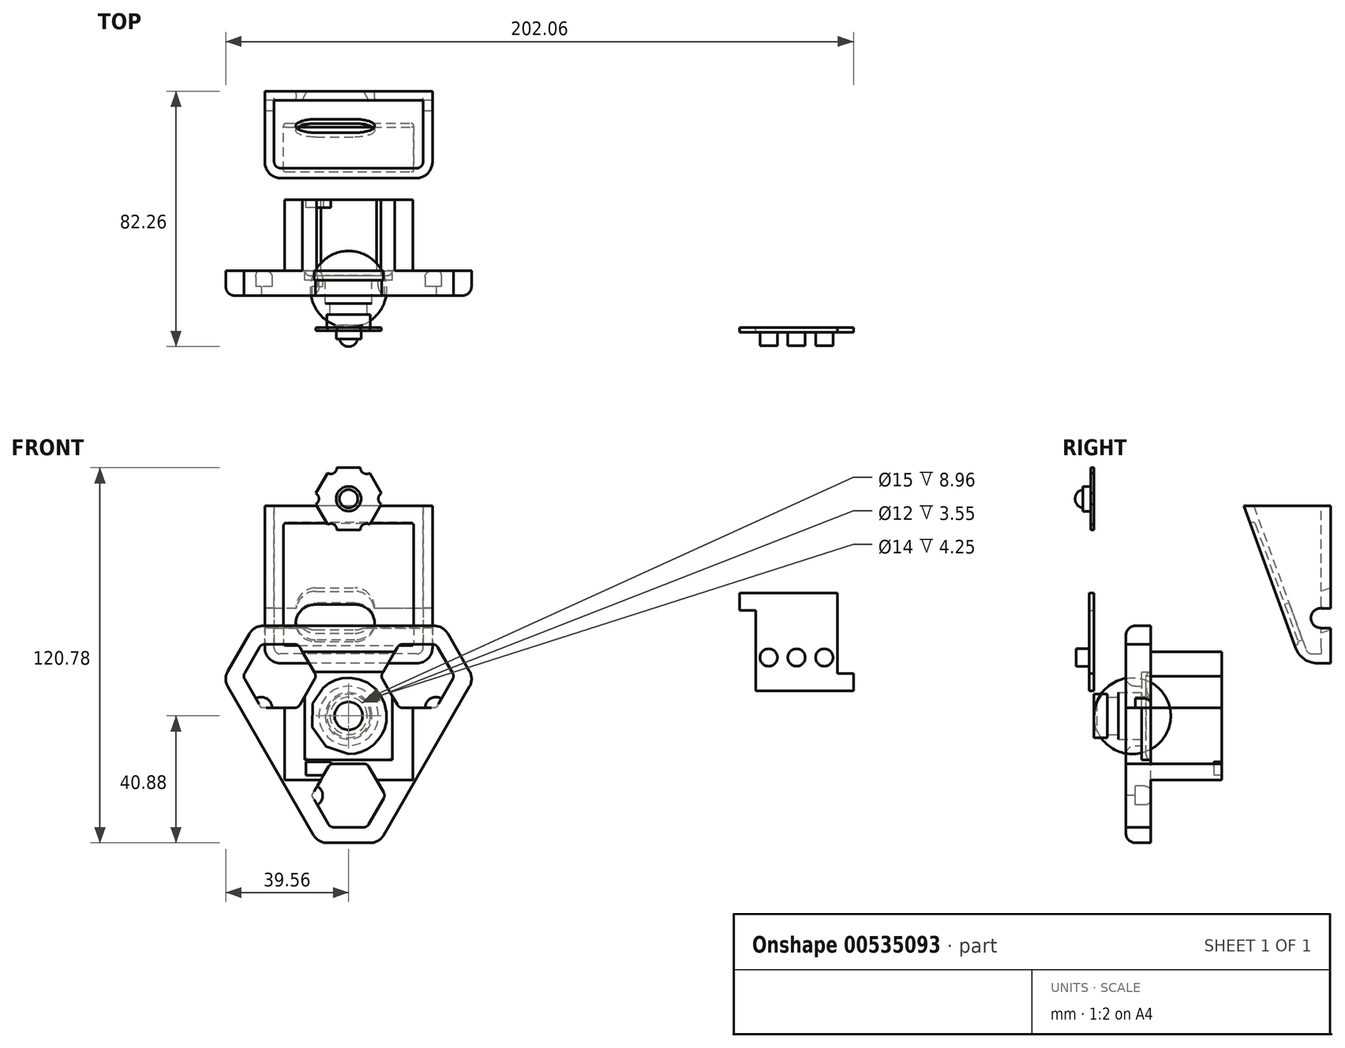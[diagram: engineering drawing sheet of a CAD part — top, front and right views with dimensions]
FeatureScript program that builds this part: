
annotation { "Feature Type Name" : "Feature", "Feature Type Description" : "" }
export const myFeature = defineFeature(function(context is Context, id is Id, definition is map)
    precondition{}
    {
        {
            var Q0;
            Q0=qCreatedBy(makeId("Right.planeOp"),FACE);
            var sketch = newSketch(context, id + "F0", { "sketchPlane" : qUnion([Q0])});
            skLineSegment(sketch, "E0", {"start": v(0, 4.5) * mm, "end": v(0, 7) * mm});
            skLineSegment(sketch, "E1", {"start": v(0, 7) * mm, "end": v(4.25, 7) * mm});
            skLineSegment(sketch, "E2", {"start": v(4.25, 7) * mm, "end": v(4.25, 6) * mm});
            skLineSegment(sketch, "E3", {"start": v(4.25, 6) * mm, "end": v(7.8, 6) * mm});
            skLineSegment(sketch, "E4", {"start": v(7.8, 6) * mm, "end": v(7.8, 7.5) * mm});
            skLineSegment(sketch, "E5", {"start": v(7.8, 7.5) * mm, "end": v(16.76, 7.5) * mm});
            skLineSegment(sketch, "E6", {"start": v(16.76, 7.5) * mm, "end": v(16.76, 0) * mm});
            skLineSegment(sketch, "E7", {"start": v(16.76, 0) * mm, "end": v(0, 0) * mm});
            skArc(sketch, "E8", {"start": v(0, 0) * mm, "mid": v(0.2, 2.29) * mm, "end": v(0.82, 4.5) * mm});
            skLineSegment(sketch, "E9", {"start": v(0.82, 4.5) * mm, "end": v(0, 4.5) * mm});
            skSolve(sketch);
        }
        {
            var Q0;
            Q0=qSketchRegion(id+"F0",true);
            var Q1;
            Q1=sQuery(id+"F0.wireOp",EDGE,"E7");
            revolve(context, id + "F1", {"entities" : qUnion([Q0]), "axis" : qUnion([Q1]), "revolveType" : RevolveType.FULL});
        }
        {
            var Q0;
            Q0=makeQuery(id+"F1.opRevolve","SWEPT_FACE",FACE,{"disambiguationData":[OSD([sQuery(id+"F0.wireOp",EDGE,"E6")])]});
            var sketch = newSketch(context, id + "F2", { "sketchPlane" : qUnion([Q0])});
            skLineSegment(sketch, "E10.bottom", {"start": v(14.1, -14.1) * mm, "end": v(-14.1, -14.1) * mm});
            skLineSegment(sketch, "E10.top", {"start": v(14.1, 14.1) * mm, "end": v(-14.1, 14.1) * mm});
            skLineSegment(sketch, "E10.left", {"start": v(14.1, -14.1) * mm, "end": v(14.1, 14.1) * mm});
            skLineSegment(sketch, "E10.right", {"start": v(-14.1, -14.1) * mm, "end": v(-14.1, 14.1) * mm});
            skPoint(sketch, "E10.middle", {"position": v(0, 0) * mm});
            skSolve(sketch);
        }
        {
            var Q0;
            Q0=qSketchRegion(id+"F2",true);
            extrude(context, id + "F3", {"entities" : qUnion([Q0]), "operationType" : NewBodyOperationType.ADD, "depth" : 1.5 * mm});
        }
        {
            var Q0;
            Q0=qCreatedBy(makeId("Front.planeOp"),FACE);
            var sketch = newSketch(context, id + "F4", { "sketchPlane" : qUnion([Q0])});
            skCircle(sketch, "E11.cCircle", {"center": v(0, 69.9) * mm, "radius": 11.55 * mm, "construction": true});
            skLineSegment(sketch, "E11.0", {"start": v(5.77, 59.9) * mm, "end": v(-5.77, 59.9) * mm});
            skLineSegment(sketch, "E11.1", {"start": v(-5.77, 59.9) * mm, "end": v(-11.55, 69.9) * mm});
            skLineSegment(sketch, "E11.2", {"start": v(-11.55, 69.9) * mm, "end": v(-5.77, 79.9) * mm});
            skLineSegment(sketch, "E11.3", {"start": v(-5.77, 79.9) * mm, "end": v(5.77, 79.9) * mm});
            skLineSegment(sketch, "E11.4", {"start": v(5.77, 79.9) * mm, "end": v(11.55, 69.9) * mm});
            skLineSegment(sketch, "E11.5", {"start": v(11.55, 69.9) * mm, "end": v(5.77, 59.9) * mm});
            skCircle(sketch, "E12", {"center": v(-5.77, 79.9) * mm, "radius": 2 * mm});
            skCircle(sketch, "E13", {"center": v(5.77, 79.9) * mm, "radius": 2 * mm});
            skCircle(sketch, "E14", {"center": v(11.55, 69.9) * mm, "radius": 2 * mm});
            skCircle(sketch, "E15", {"center": v(5.77, 59.9) * mm, "radius": 2 * mm});
            skCircle(sketch, "E16", {"center": v(-5.77, 59.9) * mm, "radius": 2 * mm});
            skCircle(sketch, "E17", {"center": v(-11.55, 69.9) * mm, "radius": 2 * mm});
            skSolve(sketch);
        }
        {
            var Q0;
            {var subQ13=sQuery(id+"F4.wireOp",EDGE,"E15");var subQ15=sQuery(id+"F4.wireOp",EDGE,"E11.0");var subQ16=makeQuery(id+"F4.imprint","INTERSECT",VERTEX,{"derivedFrom":[subQ15,subQ13]});Q0=makeQuery(id+"F4.imprint","IMPRINT",FACE,{"disambiguationData":[TD([[makeQuery(id+"F4.imprint","IMPRINT",EDGE,{"disambiguationData":[TD([[subQ16,-1.0]])],"derivedFrom":subQ15}),-1.0]])]});}
            extrude(context, id + "F5", {"entities" : qUnion([Q0]), "depth" : 1.02 * mm});
        }
        {
            var Q0;
            Q0=makeQuery(id+"F3.opExtrude","CAP_FACE",FACE,{"disambiguationData":[OSD([sQuery(id+"F2.wireOp",EDGE,"E10.bottom"),sQuery(id+"F2.wireOp",EDGE,"E10.top"),sQuery(id+"F2.wireOp",EDGE,"E10.left"),sQuery(id+"F2.wireOp",EDGE,"E10.right")])],"isStart":false});
            var sketch = newSketch(context, id + "F6", { "sketchPlane" : qUnion([Q0])});
            skLineSegment(sketch, "E18.bottom", {"start": v(-20.64, -20.64) * mm, "end": v(20.64, -20.64) * mm});
            skLineSegment(sketch, "E18.top", {"start": v(-20.64, 20.64) * mm, "end": v(20.64, 20.64) * mm});
            skLineSegment(sketch, "E18.left", {"start": v(-20.64, -20.64) * mm, "end": v(-20.64, 20.64) * mm});
            skLineSegment(sketch, "E18.right", {"start": v(20.64, -20.64) * mm, "end": v(20.64, 20.64) * mm});
            skPoint(sketch, "E18.middle", {"position": v(0, 0) * mm});
            skSolve(sketch);
        }
        {
            var Q0;
            Q0=qSketchRegion(id+"F6",true);
            extrude(context, id + "F7", {"entities" : qUnion([Q0]), "operationType" : NewBodyOperationType.ADD, "depth" : 22.86 * mm});
        }
        {
            var Q0;
            Q0=makeQuery(id+"F3.opExtrude","SWEPT_EDGE",EDGE,{"disambiguationData":[OSD([sQuery(id+"F2.wireOp",EDGE,"E10.top"),sQuery(id+"F2.wireOp",EDGE,"E10.right")])]});
            var Q1;
            Q1=makeQuery(id+"F3.opExtrude","SWEPT_EDGE",EDGE,{"disambiguationData":[OSD([sQuery(id+"F2.wireOp",EDGE,"E10.top"),sQuery(id+"F2.wireOp",EDGE,"E10.left")])]});
            var Q2;
            Q2=makeQuery(id+"F3.opExtrude","SWEPT_EDGE",EDGE,{"disambiguationData":[OSD([sQuery(id+"F2.wireOp",EDGE,"E10.bottom"),sQuery(id+"F2.wireOp",EDGE,"E10.right")])]});
            var Q3;
            Q3=makeQuery(id+"F3.opExtrude","SWEPT_EDGE",EDGE,{"disambiguationData":[OSD([sQuery(id+"F2.wireOp",EDGE,"E10.bottom"),sQuery(id+"F2.wireOp",EDGE,"E10.left")])]});
            fillet(context, id + "F8", {"entities" : qUnion([Q0, Q1, Q2, Q3]), "radius" : 1.59 * mm, "tangentPropagation" : true, "allowEdgeOverflow" : false});
        }
        {
            var Q0;
            Q0=makeQuery(id+"F3.opExtrude","CAP_EDGE",EDGE,{"disambiguationData":[OSD([sQuery(id+"F2.wireOp",EDGE,"E10.bottom")])],"isStart":true});
            fillet(context, id + "F9", {"entities" : qUnion([Q0]), "radius" : 1.59 * mm, "tangentPropagation" : true, "allowEdgeOverflow" : false});
        }
        {
            var Q0;
            Q0=makeQuery(id+"F7.opExtrude","CAP_FACE",FACE,{"disambiguationData":[OSD([sQuery(id+"F6.wireOp",EDGE,"E18.bottom"),sQuery(id+"F6.wireOp",EDGE,"E18.top"),sQuery(id+"F6.wireOp",EDGE,"E18.left"),sQuery(id+"F6.wireOp",EDGE,"E18.right")])],"isStart":false});
            var sketch = newSketch(context, id + "F10", { "sketchPlane" : qUnion([Q0])});
            skLineSegment(sketch, "E19.bottom", {"start": v(5.69, -14.77) * mm, "end": v(13.73, -14.77) * mm});
            skLineSegment(sketch, "E19.top", {"start": v(5.69, -19.15) * mm, "end": v(13.73, -19.15) * mm});
            skLineSegment(sketch, "E19.left", {"start": v(5.69, -14.77) * mm, "end": v(5.69, -19.15) * mm});
            skLineSegment(sketch, "E19.right", {"start": v(13.73, -14.77) * mm, "end": v(13.73, -19.15) * mm});
            skSolve(sketch);
        }
        {
            var Q0;
            Q0=qSketchRegion(id+"F10",true);
            extrude(context, id + "F11", {"entities" : qUnion([Q0]), "operationType" : NewBodyOperationType.REMOVE, "oppositeDirection" : true, "depth" : 2.54 * mm});
        }
        {
            var Q0;
            Q0=qCreatedBy(makeId("Right.planeOp"),FACE);
            var sketch = newSketch(context, id + "F12", { "sketchPlane" : qUnion([Q0])});
            skLineSegment(sketch, "E20", {"start": v(-6.12, 69.9) * mm, "end": v(-1.02, 69.9) * mm});
            skLineSegment(sketch, "E21", {"start": v(-1.02, 69.9) * mm, "end": v(-1.02, 73.9) * mm});
            skLineSegment(sketch, "E22", {"start": v(-1.02, 73.9) * mm, "end": v(-3.62, 73.9) * mm});
            skLineSegment(sketch, "E23", {"start": v(-3.62, 73.9) * mm, "end": v(-3.62, 72.85) * mm});
            skArc(sketch, "E24", {"start": v(-6.12, 69.9) * mm, "mid": v(-5.4, 71.83) * mm, "end": v(-3.62, 72.85) * mm});
            skSolve(sketch);
        }
        {
            var Q0;
            Q0=makeQuery(id+"F12.imprint","IMPRINT",FACE,{"disambiguationData":[TD([[makeQuery(id+"F12.imprint","IMPRINT",EDGE,{"derivedFrom":sQuery(id+"F12.wireOp",EDGE,"E20")}),1.0]])]});
            var Q1;
            Q1=sQuery(id+"F12.wireOp",EDGE,"E20");
            revolve(context, id + "F13", {"operationType" : NewBodyOperationType.ADD, "entities" : qUnion([Q0]), "axis" : qUnion([Q1]), "revolveType" : RevolveType.FULL});
        }
        {
            var Q0;
            Q0=makeQuery(id+"F7.opExtrude","CAP_FACE",FACE,{"disambiguationData":[OSD([sQuery(id+"F6.wireOp",EDGE,"E18.bottom"),sQuery(id+"F6.wireOp",EDGE,"E18.top"),sQuery(id+"F6.wireOp",EDGE,"E18.left"),sQuery(id+"F6.wireOp",EDGE,"E18.right")])],"isStart":true});
            var sketch = newSketch(context, id + "F14", { "sketchPlane" : qUnion([Q0])});
            skLineSegment(sketch, "E25.bottom", {"start": v(14.1, -14.1) * mm, "end": v(-14.1, -14.1) * mm});
            skLineSegment(sketch, "E25.top", {"start": v(14.1, 14.1) * mm, "end": v(-14.1, 14.1) * mm});
            skLineSegment(sketch, "E25.left", {"start": v(14.1, -14.1) * mm, "end": v(14.1, 14.1) * mm});
            skLineSegment(sketch, "E25.right", {"start": v(-14.1, -14.1) * mm, "end": v(-14.1, 14.1) * mm});
            skPoint(sketch, "E25.middle", {"position": v(0, 0) * mm});
            skLineSegment(sketch, "E26", {"start": v(-30.48, 28.97) * mm, "end": v(-40.33, 11.92) * mm});
            skLineSegment(sketch, "E27", {"start": v(-40.33, 11.92) * mm, "end": v(-9.84, -40.88) * mm});
            skLineSegment(sketch, "E28", {"start": v(-9.84, -40.88) * mm, "end": v(9.84, -40.88) * mm});
            skLineSegment(sketch, "E29", {"start": v(9.84, -40.88) * mm, "end": v(40.33, 11.92) * mm});
            skLineSegment(sketch, "E30", {"start": v(40.33, 11.92) * mm, "end": v(30.48, 28.97) * mm});
            skLineSegment(sketch, "E31", {"start": v(30.48, 28.97) * mm, "end": v(-30.48, 28.97) * mm});
            skLineSegment(sketch, "E32", {"start": v(-35.4, 20.44) * mm, "end": v(25.09, -14.48) * mm, "construction": true});
            skCircle(sketch, "E33.cCircle", {"center": v(-20.64, 11.92) * mm, "radius": 12.28 * mm, "construction": true});
            skLineSegment(sketch, "E33.0", {"start": v(-32.92, 11.92) * mm, "end": v(-26.78, 22.55) * mm, "construction": true});
            skLineSegment(sketch, "E33.1", {"start": v(-26.78, 22.55) * mm, "end": v(-14.5, 22.55) * mm, "construction": true});
            skLineSegment(sketch, "E33.2", {"start": v(-14.5, 22.55) * mm, "end": v(-8.36, 11.92) * mm, "construction": true});
            skLineSegment(sketch, "E33.3", {"start": v(-8.36, 11.92) * mm, "end": v(-14.5, 1.28) * mm, "construction": true});
            skLineSegment(sketch, "E33.4", {"start": v(-14.5, 1.28) * mm, "end": v(-26.78, 1.28) * mm, "construction": true});
            skLineSegment(sketch, "E33.5", {"start": v(-26.78, 1.28) * mm, "end": v(-32.92, 11.92) * mm, "construction": true});
            skLineSegment(sketch, "E34", {"start": v(-40.33, 11.92) * mm, "end": v(-20.64, 11.92) * mm, "construction": true});
            skSolve(sketch);
        }
        {
            var Q0;
            Q0=makeQuery(id+"F14.imprint","IMPRINT",FACE,{"disambiguationData":[TD([[makeQuery(id+"F14.imprint","IMPRINT",EDGE,{"derivedFrom":sQuery(id+"F14.wireOp",EDGE,"E26")}),1.0]])]});
            extrude(context, id + "F15", {"entities" : qUnion([Q0]), "depth" : 3 * mm});
        }
        {
            var Q0;
            Q0=makeQuery(id+"F15.opExtrude","CAP_FACE",FACE,{"disambiguationData":[OSD([sQuery(id+"F6.wireOp",EDGE,"E18.bottom"),sQuery(id+"F6.wireOp",EDGE,"E18.top"),sQuery(id+"F6.wireOp",EDGE,"E18.left"),sQuery(id+"F6.wireOp",EDGE,"E18.right"),sQuery(id+"F14.wireOp",EDGE,"E26"),sQuery(id+"F14.wireOp",EDGE,"E27"),sQuery(id+"F14.wireOp",EDGE,"E28"),sQuery(id+"F14.wireOp",EDGE,"E29"),sQuery(id+"F14.wireOp",EDGE,"E30"),sQuery(id+"F14.wireOp",EDGE,"E31")])],"isStart":false});
            var sketch = newSketch(context, id + "F16", { "sketchPlane" : qUnion([Q0])});
            skLineSegment(sketch, "E35.0", {"start": v(-30.48, 28.97) * mm, "end": v(-40.33, 11.92) * mm});
            skLineSegment(sketch, "E36.0", {"start": v(30.48, 28.97) * mm, "end": v(-30.48, 28.97) * mm});
            skLineSegment(sketch, "E37.0", {"start": v(-40.33, 11.92) * mm, "end": v(-9.84, -40.88) * mm});
            skLineSegment(sketch, "E38.0", {"start": v(40.33, 11.92) * mm, "end": v(30.48, 28.97) * mm});
            skLineSegment(sketch, "E39.0", {"start": v(9.84, -40.88) * mm, "end": v(40.33, 11.92) * mm});
            skLineSegment(sketch, "E40.0", {"start": v(-9.84, -40.88) * mm, "end": v(9.84, -40.88) * mm});
            skCircle(sketch, "E41", {"center": v(0, 0) * mm, "radius": 9.53 * mm});
            skSolve(sketch);
        }
        {
            var Q0;
            Q0=qSketchRegion(id+"F16",true);
            var Q1;
            {var subQ4=sQuery(id+"F6.wireOp",EDGE,"E18.bottom");Q1=makeQuery(id+"F14.imprint","IMPRINT",FACE,{"disambiguationData":[TD([[makeQuery(id+"F14.imprint","IMPRINT",EDGE,{"derivedFrom":makeQuery(id+"F7.opExtrude","CAP_EDGE",EDGE,{"disambiguationData":[OSD([subQ4])],"isStart":true})}),-1.0]])]});}
            extrude(context, id + "F17", {"entities" : qUnion([Q0, Q1]), "operationType" : NewBodyOperationType.ADD, "depth" : 5 * mm, "offsetDistance" : 25.4 * mm});
        }
        {
            var Q0;
            Q0=makeQuery(id+"F17.opExtrude","CAP_FACE",FACE,{"disambiguationData":[OSD([sQuery(id+"F16.wireOp",EDGE,"E35.0"),sQuery(id+"F16.wireOp",EDGE,"E36.0"),sQuery(id+"F16.wireOp",EDGE,"E37.0"),sQuery(id+"F16.wireOp",EDGE,"E38.0"),sQuery(id+"F16.wireOp",EDGE,"E39.0"),sQuery(id+"F16.wireOp",EDGE,"E40.0"),sQuery(id+"F16.wireOp",EDGE,"E41")])],"isStart":false});
            var sketch = newSketch(context, id + "F18", { "sketchPlane" : qUnion([Q0])});
            skCircle(sketch, "E42.cCircle", {"center": v(-22.2, 12.82) * mm, "radius": 11.84 * mm, "construction": true});
            skLineSegment(sketch, "E42.0", {"start": v(-34.04, 12.82) * mm, "end": v(-28.12, 23.07) * mm});
            skLineSegment(sketch, "E42.1", {"start": v(-28.12, 23.07) * mm, "end": v(-16.28, 23.07) * mm});
            skLineSegment(sketch, "E42.2", {"start": v(-16.28, 23.07) * mm, "end": v(-10.36, 12.82) * mm});
            skLineSegment(sketch, "E42.3", {"start": v(-10.36, 12.82) * mm, "end": v(-16.28, 2.57) * mm});
            skLineSegment(sketch, "E42.4", {"start": v(-16.28, 2.57) * mm, "end": v(-28.12, 2.57) * mm});
            skLineSegment(sketch, "E42.5", {"start": v(-28.12, 2.57) * mm, "end": v(-34.04, 12.82) * mm});
            skLineSegment(sketch, "E43", {"start": v(-35.4, 20.44) * mm, "end": v(25.09, -14.48) * mm, "construction": true});
            skCircle(sketch, "E44.cCircle", {"center": v(22.2, 12.82) * mm, "radius": 11.84 * mm, "construction": true});
            skLineSegment(sketch, "E44.0", {"start": v(16.28, 23.07) * mm, "end": v(28.12, 23.07) * mm});
            skLineSegment(sketch, "E44.1", {"start": v(28.12, 23.07) * mm, "end": v(34.04, 12.82) * mm});
            skLineSegment(sketch, "E44.2", {"start": v(34.04, 12.82) * mm, "end": v(28.12, 2.57) * mm});
            skLineSegment(sketch, "E44.3", {"start": v(28.12, 2.57) * mm, "end": v(16.28, 2.57) * mm});
            skLineSegment(sketch, "E44.4", {"start": v(16.28, 2.57) * mm, "end": v(10.36, 12.82) * mm});
            skLineSegment(sketch, "E44.5", {"start": v(10.36, 12.82) * mm, "end": v(16.28, 23.07) * mm});
            skCircle(sketch, "E45.cCircle", {"center": v(0, -25.63) * mm, "radius": 11.84 * mm, "construction": true});
            skLineSegment(sketch, "E45.0", {"start": v(11.84, -25.63) * mm, "end": v(5.92, -35.88) * mm});
            skLineSegment(sketch, "E45.1", {"start": v(5.92, -35.88) * mm, "end": v(-5.92, -35.88) * mm});
            skLineSegment(sketch, "E45.2", {"start": v(-5.92, -35.88) * mm, "end": v(-11.84, -25.63) * mm});
            skLineSegment(sketch, "E45.3", {"start": v(-11.84, -25.63) * mm, "end": v(-5.92, -15.38) * mm});
            skLineSegment(sketch, "E45.4", {"start": v(-5.92, -15.38) * mm, "end": v(5.92, -15.38) * mm});
            skLineSegment(sketch, "E45.5", {"start": v(5.92, -15.38) * mm, "end": v(11.84, -25.63) * mm});
            skArc(sketch, "E46", {"start": v(-19.78, 23.07) * mm, "mid": v(-18.03, 20.04) * mm, "end": v(-14.53, 20.04) * mm});
            skArc(sketch, "E47", {"start": v(-29.87, 5.6) * mm, "mid": v(-26.37, 5.6) * mm, "end": v(-24.62, 2.57) * mm});
            skArc(sketch, "E48", {"start": v(14.53, 20.04) * mm, "mid": v(18.03, 20.04) * mm, "end": v(19.78, 23.07) * mm});
            skArc(sketch, "E49", {"start": v(24.62, 2.57) * mm, "mid": v(26.37, 5.6) * mm, "end": v(29.87, 5.6) * mm});
            skArc(sketch, "E50", {"start": v(10.09, -22.6) * mm, "mid": v(8.34, -25.63) * mm, "end": v(10.09, -28.66) * mm});
            skArc(sketch, "E51", {"start": v(-10.09, -22.6) * mm, "mid": v(-8.34, -25.63) * mm, "end": v(-10.09, -28.66) * mm});
            skSolve(sketch);
        }
        {
            var Q0;
            Q0=qSketchRegion(id+"F18",true);
            extrude(context, id + "F19", {"entities" : qUnion([Q0]), "operationType" : NewBodyOperationType.REMOVE, "oppositeDirection" : true, "depth" : 3 * mm});
        }
        {
            var Q0;
            {var subQ3=sQuery(id+"F18.wireOp",EDGE,"E46");Q0=makeQuery(id+"F18.imprint","IMPRINT",FACE,{"disambiguationData":[TD([[makeQuery(id+"F18.imprint","IMPRINT",EDGE,{"derivedFrom":subQ3}),1.0]])]});}
            var Q1;
            {var subQ3=sQuery(id+"F18.wireOp",EDGE,"E47");Q1=makeQuery(id+"F18.imprint","IMPRINT",FACE,{"disambiguationData":[TD([[makeQuery(id+"F18.imprint","IMPRINT",EDGE,{"derivedFrom":subQ3}),-1.0]])]});}
            var Q2;
            {var subQ3=sQuery(id+"F18.wireOp",EDGE,"E48");Q2=makeQuery(id+"F18.imprint","IMPRINT",FACE,{"disambiguationData":[TD([[makeQuery(id+"F18.imprint","IMPRINT",EDGE,{"derivedFrom":subQ3}),1.0]])]});}
            var Q3;
            {var subQ3=sQuery(id+"F18.wireOp",EDGE,"E49");Q3=makeQuery(id+"F18.imprint","IMPRINT",FACE,{"disambiguationData":[TD([[makeQuery(id+"F18.imprint","IMPRINT",EDGE,{"derivedFrom":subQ3}),-1.0]])]});}
            var Q4;
            {var subQ3=sQuery(id+"F18.wireOp",EDGE,"E50");Q4=makeQuery(id+"F18.imprint","IMPRINT",FACE,{"disambiguationData":[TD([[makeQuery(id+"F18.imprint","IMPRINT",EDGE,{"derivedFrom":subQ3}),1.0]])]});}
            var Q5;
            {var subQ3=sQuery(id+"F18.wireOp",EDGE,"E51");Q5=makeQuery(id+"F18.imprint","IMPRINT",FACE,{"disambiguationData":[TD([[makeQuery(id+"F18.imprint","IMPRINT",EDGE,{"derivedFrom":subQ3}),-1.0]])]});}
            extrude(context, id + "F20", {"entities" : qUnion([Q0, Q1, Q2, Q3, Q4, Q5]), "operationType" : NewBodyOperationType.REMOVE, "endBound" : BoundingType.THROUGH_ALL, "oppositeDirection" : true, "depth" : 25.4 * mm});
        }
        {
            var Q0;
            Q0=makeQuery(id+"F17.boolean.opBoolean","MERGE",EDGE,{"derivedFrom":[makeQuery(id+"F15.opExtrude","SWEPT_EDGE",EDGE,{"disambiguationData":[OSD([sQuery(id+"F14.wireOp",EDGE,"E26"),sQuery(id+"F14.wireOp",EDGE,"E31")])]}),makeQuery(id+"F17.opExtrude","SWEPT_EDGE",EDGE,{"disambiguationData":[OSD([sQuery(id+"F16.wireOp",EDGE,"E35.0"),sQuery(id+"F16.wireOp",EDGE,"E36.0")])]})]});
            var Q1;
            Q1=makeQuery(id+"F17.boolean.opBoolean","MERGE",EDGE,{"derivedFrom":[makeQuery(id+"F15.opExtrude","SWEPT_EDGE",EDGE,{"disambiguationData":[OSD([sQuery(id+"F14.wireOp",EDGE,"E26"),sQuery(id+"F14.wireOp",EDGE,"E27")])]}),makeQuery(id+"F17.opExtrude","SWEPT_EDGE",EDGE,{"disambiguationData":[OSD([sQuery(id+"F16.wireOp",EDGE,"E35.0"),sQuery(id+"F16.wireOp",EDGE,"E37.0")])]})]});
            var Q2;
            Q2=makeQuery(id+"F17.boolean.opBoolean","MERGE",EDGE,{"derivedFrom":[makeQuery(id+"F15.opExtrude","SWEPT_EDGE",EDGE,{"disambiguationData":[OSD([sQuery(id+"F14.wireOp",EDGE,"E30"),sQuery(id+"F14.wireOp",EDGE,"E31")])]}),makeQuery(id+"F17.opExtrude","SWEPT_EDGE",EDGE,{"disambiguationData":[OSD([sQuery(id+"F16.wireOp",EDGE,"E36.0"),sQuery(id+"F16.wireOp",EDGE,"E38.0")])]})]});
            var Q3;
            Q3=makeQuery(id+"F17.boolean.opBoolean","MERGE",EDGE,{"derivedFrom":[makeQuery(id+"F15.opExtrude","SWEPT_EDGE",EDGE,{"disambiguationData":[OSD([sQuery(id+"F14.wireOp",EDGE,"E29"),sQuery(id+"F14.wireOp",EDGE,"E30")])]}),makeQuery(id+"F17.opExtrude","SWEPT_EDGE",EDGE,{"disambiguationData":[OSD([sQuery(id+"F16.wireOp",EDGE,"E38.0"),sQuery(id+"F16.wireOp",EDGE,"E39.0")])]})]});
            var Q4;
            Q4=makeQuery(id+"F17.boolean.opBoolean","MERGE",EDGE,{"derivedFrom":[makeQuery(id+"F15.opExtrude","SWEPT_EDGE",EDGE,{"disambiguationData":[OSD([sQuery(id+"F14.wireOp",EDGE,"E28"),sQuery(id+"F14.wireOp",EDGE,"E29")])]}),makeQuery(id+"F17.opExtrude","SWEPT_EDGE",EDGE,{"disambiguationData":[OSD([sQuery(id+"F16.wireOp",EDGE,"E39.0"),sQuery(id+"F16.wireOp",EDGE,"E40.0")])]})]});
            var Q5;
            Q5=makeQuery(id+"F17.boolean.opBoolean","MERGE",EDGE,{"derivedFrom":[makeQuery(id+"F15.opExtrude","SWEPT_EDGE",EDGE,{"disambiguationData":[OSD([sQuery(id+"F14.wireOp",EDGE,"E27"),sQuery(id+"F14.wireOp",EDGE,"E28")])]}),makeQuery(id+"F17.opExtrude","SWEPT_EDGE",EDGE,{"disambiguationData":[OSD([sQuery(id+"F16.wireOp",EDGE,"E37.0"),sQuery(id+"F16.wireOp",EDGE,"E40.0")])]})]});
            fillet(context, id + "F21", {"entities" : qUnion([Q0, Q1, Q2, Q3, Q4, Q5]), "radius" : 5 * mm, "tangentPropagation" : true, "allowEdgeOverflow" : false});
        }
        {
            var Q0;
            Q0=makeQuery(id+"F19.boolean.opBoolean","COPY",EDGE,{"derivedFrom":makeQuery(id+"F19.opExtrude","SWEPT_EDGE",EDGE,{"disambiguationData":[OSD([sQuery(id+"F18.wireOp",EDGE,"E42.0"),sQuery(id+"F18.wireOp",EDGE,"E42.1")])]})});
            var Q1;
            Q1=makeQuery(id+"F19.boolean.opBoolean","COPY",EDGE,{"derivedFrom":makeQuery(id+"F19.opExtrude","SWEPT_EDGE",EDGE,{"disambiguationData":[OSD([sQuery(id+"F18.wireOp",EDGE,"E42.0"),sQuery(id+"F18.wireOp",EDGE,"E42.5")])]})});
            var Q2;
            {var subQ0=sQuery(id+"F18.wireOp",EDGE,"E42.5");var subQ1=sQuery(id+"F18.wireOp",EDGE,"E42.4");Q2=makeQuery(id+"F20.boolean.opBoolean","MERGE",EDGE,{"derivedFrom":[makeQuery(id+"F19.boolean.opBoolean","COPY",EDGE,{"derivedFrom":makeQuery(id+"F19.opExtrude","SWEPT_EDGE",EDGE,{"disambiguationData":[OSD([subQ1,subQ0])]})}),makeQuery(id+"F20.opExtrude","SWEPT_EDGE",EDGE,{"disambiguationData":[OSD([subQ1,subQ0])]})]});}
            var Q3;
            Q3=makeQuery(id+"F19.boolean.opBoolean","COPY",EDGE,{"derivedFrom":makeQuery(id+"F19.opExtrude","SWEPT_EDGE",EDGE,{"disambiguationData":[OSD([sQuery(id+"F18.wireOp",EDGE,"E42.3"),sQuery(id+"F18.wireOp",EDGE,"E42.4")])]})});
            var Q4;
            Q4=makeQuery(id+"F19.boolean.opBoolean","COPY",EDGE,{"derivedFrom":makeQuery(id+"F19.opExtrude","SWEPT_EDGE",EDGE,{"disambiguationData":[OSD([sQuery(id+"F18.wireOp",EDGE,"E42.2"),sQuery(id+"F18.wireOp",EDGE,"E42.3")])]})});
            var Q5;
            {var subQ0=sQuery(id+"F18.wireOp",EDGE,"E42.2");var subQ1=sQuery(id+"F18.wireOp",EDGE,"E42.1");Q5=makeQuery(id+"F20.boolean.opBoolean","MERGE",EDGE,{"derivedFrom":[makeQuery(id+"F19.boolean.opBoolean","COPY",EDGE,{"derivedFrom":makeQuery(id+"F19.opExtrude","SWEPT_EDGE",EDGE,{"disambiguationData":[OSD([subQ1,subQ0])]})}),makeQuery(id+"F20.opExtrude","SWEPT_EDGE",EDGE,{"disambiguationData":[OSD([subQ1,subQ0])]})]});}
            var Q6;
            Q6=makeQuery(id+"F19.boolean.opBoolean","COPY",EDGE,{"derivedFrom":makeQuery(id+"F19.opExtrude","SWEPT_EDGE",EDGE,{"disambiguationData":[OSD([sQuery(id+"F18.wireOp",EDGE,"E45.3"),sQuery(id+"F18.wireOp",EDGE,"E45.4")])]})});
            var Q7;
            {var subQ0=sQuery(id+"F18.wireOp",EDGE,"E45.3");var subQ1=sQuery(id+"F18.wireOp",EDGE,"E45.2");Q7=makeQuery(id+"F20.boolean.opBoolean","MERGE",EDGE,{"derivedFrom":[makeQuery(id+"F19.boolean.opBoolean","COPY",EDGE,{"derivedFrom":makeQuery(id+"F19.opExtrude","SWEPT_EDGE",EDGE,{"disambiguationData":[OSD([subQ1,subQ0])]})}),makeQuery(id+"F20.opExtrude","SWEPT_EDGE",EDGE,{"disambiguationData":[OSD([subQ1,subQ0])]})]});}
            var Q8;
            Q8=makeQuery(id+"F19.boolean.opBoolean","COPY",EDGE,{"derivedFrom":makeQuery(id+"F19.opExtrude","SWEPT_EDGE",EDGE,{"disambiguationData":[OSD([sQuery(id+"F18.wireOp",EDGE,"E45.1"),sQuery(id+"F18.wireOp",EDGE,"E45.2")])]})});
            var Q9;
            Q9=makeQuery(id+"F19.boolean.opBoolean","COPY",EDGE,{"derivedFrom":makeQuery(id+"F19.opExtrude","SWEPT_EDGE",EDGE,{"disambiguationData":[OSD([sQuery(id+"F18.wireOp",EDGE,"E45.0"),sQuery(id+"F18.wireOp",EDGE,"E45.1")])]})});
            var Q10;
            {var subQ0=sQuery(id+"F18.wireOp",EDGE,"E45.5");var subQ1=sQuery(id+"F18.wireOp",EDGE,"E45.0");Q10=makeQuery(id+"F20.boolean.opBoolean","MERGE",EDGE,{"derivedFrom":[makeQuery(id+"F19.boolean.opBoolean","COPY",EDGE,{"derivedFrom":makeQuery(id+"F19.opExtrude","SWEPT_EDGE",EDGE,{"disambiguationData":[OSD([subQ1,subQ0])]})}),makeQuery(id+"F20.opExtrude","SWEPT_EDGE",EDGE,{"disambiguationData":[OSD([subQ1,subQ0])]})]});}
            var Q11;
            Q11=makeQuery(id+"F19.boolean.opBoolean","COPY",EDGE,{"derivedFrom":makeQuery(id+"F19.opExtrude","SWEPT_EDGE",EDGE,{"disambiguationData":[OSD([sQuery(id+"F18.wireOp",EDGE,"E45.4"),sQuery(id+"F18.wireOp",EDGE,"E45.5")])]})});
            var Q12;
            Q12=makeQuery(id+"F19.boolean.opBoolean","COPY",EDGE,{"derivedFrom":makeQuery(id+"F19.opExtrude","SWEPT_EDGE",EDGE,{"disambiguationData":[OSD([sQuery(id+"F18.wireOp",EDGE,"E44.0"),sQuery(id+"F18.wireOp",EDGE,"E44.1")])]})});
            var Q13;
            {var subQ0=sQuery(id+"F18.wireOp",EDGE,"E44.5");var subQ1=sQuery(id+"F18.wireOp",EDGE,"E44.0");Q13=makeQuery(id+"F20.boolean.opBoolean","MERGE",EDGE,{"derivedFrom":[makeQuery(id+"F19.boolean.opBoolean","COPY",EDGE,{"derivedFrom":makeQuery(id+"F19.opExtrude","SWEPT_EDGE",EDGE,{"disambiguationData":[OSD([subQ1,subQ0])]})}),makeQuery(id+"F20.opExtrude","SWEPT_EDGE",EDGE,{"disambiguationData":[OSD([subQ1,subQ0])]})]});}
            var Q14;
            Q14=makeQuery(id+"F19.boolean.opBoolean","COPY",EDGE,{"derivedFrom":makeQuery(id+"F19.opExtrude","SWEPT_EDGE",EDGE,{"disambiguationData":[OSD([sQuery(id+"F18.wireOp",EDGE,"E44.4"),sQuery(id+"F18.wireOp",EDGE,"E44.5")])]})});
            var Q15;
            Q15=makeQuery(id+"F19.boolean.opBoolean","COPY",EDGE,{"derivedFrom":makeQuery(id+"F19.opExtrude","SWEPT_EDGE",EDGE,{"disambiguationData":[OSD([sQuery(id+"F18.wireOp",EDGE,"E44.3"),sQuery(id+"F18.wireOp",EDGE,"E44.4")])]})});
            var Q16;
            {var subQ0=sQuery(id+"F18.wireOp",EDGE,"E44.3");var subQ1=sQuery(id+"F18.wireOp",EDGE,"E44.2");Q16=makeQuery(id+"F20.boolean.opBoolean","MERGE",EDGE,{"derivedFrom":[makeQuery(id+"F19.boolean.opBoolean","COPY",EDGE,{"derivedFrom":makeQuery(id+"F19.opExtrude","SWEPT_EDGE",EDGE,{"disambiguationData":[OSD([subQ1,subQ0])]})}),makeQuery(id+"F20.opExtrude","SWEPT_EDGE",EDGE,{"disambiguationData":[OSD([subQ1,subQ0])]})]});}
            var Q17;
            Q17=makeQuery(id+"F19.boolean.opBoolean","COPY",EDGE,{"derivedFrom":makeQuery(id+"F19.opExtrude","SWEPT_EDGE",EDGE,{"disambiguationData":[OSD([sQuery(id+"F18.wireOp",EDGE,"E44.1"),sQuery(id+"F18.wireOp",EDGE,"E44.2")])]})});
            fillet(context, id + "F22", {"entities" : qUnion([Q0, Q1, Q2, Q3, Q4, Q5, Q6, Q7, Q8, Q9, Q10, Q11, Q12, Q13, Q14, Q15, Q16, Q17]), "radius" : 2 * mm, "tangentPropagation" : true, "allowEdgeOverflow" : false});
        }
        {
            var Q0;
            Q0=makeQuery(id+"F17.opExtrude","CAP_EDGE",EDGE,{"disambiguationData":[OSD([sQuery(id+"F16.wireOp",EDGE,"E38.0")])],"isStart":false});
            var Q1;
            Q1=makeQuery(id+"F17.opExtrude","CAP_EDGE",EDGE,{"disambiguationData":[OSD([sQuery(id+"F16.wireOp",EDGE,"E41")])],"isStart":false});
            fillet(context, id + "F23", {"entities" : qUnion([Q0, Q1]), "radius" : 3 * mm, "tangentPropagation" : true, "allowEdgeOverflow" : false});
        }
        {
            var Q0;
            Q0=makeQuery(id+"F20.boolean.opBoolean","INTERSECT",EDGE,{"derivedFrom":[makeQuery(id+"F15.opExtrude","CAP_FACE",FACE,{"disambiguationData":[OSD([sQuery(id+"F6.wireOp",EDGE,"E18.bottom"),sQuery(id+"F6.wireOp",EDGE,"E18.top"),sQuery(id+"F6.wireOp",EDGE,"E18.left"),sQuery(id+"F6.wireOp",EDGE,"E18.right"),sQuery(id+"F14.wireOp",EDGE,"E26"),sQuery(id+"F14.wireOp",EDGE,"E27"),sQuery(id+"F14.wireOp",EDGE,"E28"),sQuery(id+"F14.wireOp",EDGE,"E29"),sQuery(id+"F14.wireOp",EDGE,"E30"),sQuery(id+"F14.wireOp",EDGE,"E31")])],"isStart":true}),makeQuery(id+"F20.opExtrude","SWEPT_FACE",FACE,{"disambiguationData":[OSD([sQuery(id+"F18.wireOp",EDGE,"E47")])]})]});
            var Q1;
            Q1=makeQuery(id+"F20.boolean.opBoolean","INTERSECT",EDGE,{"derivedFrom":[makeQuery(id+"F15.opExtrude","CAP_FACE",FACE,{"disambiguationData":[OSD([sQuery(id+"F6.wireOp",EDGE,"E18.bottom"),sQuery(id+"F6.wireOp",EDGE,"E18.top"),sQuery(id+"F6.wireOp",EDGE,"E18.left"),sQuery(id+"F6.wireOp",EDGE,"E18.right"),sQuery(id+"F14.wireOp",EDGE,"E26"),sQuery(id+"F14.wireOp",EDGE,"E27"),sQuery(id+"F14.wireOp",EDGE,"E28"),sQuery(id+"F14.wireOp",EDGE,"E29"),sQuery(id+"F14.wireOp",EDGE,"E30"),sQuery(id+"F14.wireOp",EDGE,"E31")])],"isStart":true}),makeQuery(id+"F20.opExtrude","SWEPT_FACE",FACE,{"disambiguationData":[OSD([sQuery(id+"F18.wireOp",EDGE,"E46")])]})]});
            var Q2;
            Q2=makeQuery(id+"F20.boolean.opBoolean","INTERSECT",EDGE,{"derivedFrom":[makeQuery(id+"F15.opExtrude","CAP_FACE",FACE,{"disambiguationData":[OSD([sQuery(id+"F6.wireOp",EDGE,"E18.bottom"),sQuery(id+"F6.wireOp",EDGE,"E18.top"),sQuery(id+"F6.wireOp",EDGE,"E18.left"),sQuery(id+"F6.wireOp",EDGE,"E18.right"),sQuery(id+"F14.wireOp",EDGE,"E26"),sQuery(id+"F14.wireOp",EDGE,"E27"),sQuery(id+"F14.wireOp",EDGE,"E28"),sQuery(id+"F14.wireOp",EDGE,"E29"),sQuery(id+"F14.wireOp",EDGE,"E30"),sQuery(id+"F14.wireOp",EDGE,"E31")])],"isStart":true}),makeQuery(id+"F20.opExtrude","SWEPT_FACE",FACE,{"disambiguationData":[OSD([sQuery(id+"F18.wireOp",EDGE,"E48")])]})]});
            var Q3;
            Q3=makeQuery(id+"F20.boolean.opBoolean","INTERSECT",EDGE,{"derivedFrom":[makeQuery(id+"F15.opExtrude","CAP_FACE",FACE,{"disambiguationData":[OSD([sQuery(id+"F6.wireOp",EDGE,"E18.bottom"),sQuery(id+"F6.wireOp",EDGE,"E18.top"),sQuery(id+"F6.wireOp",EDGE,"E18.left"),sQuery(id+"F6.wireOp",EDGE,"E18.right"),sQuery(id+"F14.wireOp",EDGE,"E26"),sQuery(id+"F14.wireOp",EDGE,"E27"),sQuery(id+"F14.wireOp",EDGE,"E28"),sQuery(id+"F14.wireOp",EDGE,"E29"),sQuery(id+"F14.wireOp",EDGE,"E30"),sQuery(id+"F14.wireOp",EDGE,"E31")])],"isStart":true}),makeQuery(id+"F20.opExtrude","SWEPT_FACE",FACE,{"disambiguationData":[OSD([sQuery(id+"F18.wireOp",EDGE,"E49")])]})]});
            var Q4;
            Q4=makeQuery(id+"F20.boolean.opBoolean","INTERSECT",EDGE,{"derivedFrom":[makeQuery(id+"F15.opExtrude","CAP_FACE",FACE,{"disambiguationData":[OSD([sQuery(id+"F6.wireOp",EDGE,"E18.bottom"),sQuery(id+"F6.wireOp",EDGE,"E18.top"),sQuery(id+"F6.wireOp",EDGE,"E18.left"),sQuery(id+"F6.wireOp",EDGE,"E18.right"),sQuery(id+"F14.wireOp",EDGE,"E26"),sQuery(id+"F14.wireOp",EDGE,"E27"),sQuery(id+"F14.wireOp",EDGE,"E28"),sQuery(id+"F14.wireOp",EDGE,"E29"),sQuery(id+"F14.wireOp",EDGE,"E30"),sQuery(id+"F14.wireOp",EDGE,"E31")])],"isStart":true}),makeQuery(id+"F20.opExtrude","SWEPT_FACE",FACE,{"disambiguationData":[OSD([sQuery(id+"F18.wireOp",EDGE,"E51")])]})]});
            var Q5;
            Q5=makeQuery(id+"F20.boolean.opBoolean","INTERSECT",EDGE,{"derivedFrom":[makeQuery(id+"F15.opExtrude","CAP_FACE",FACE,{"disambiguationData":[OSD([sQuery(id+"F6.wireOp",EDGE,"E18.bottom"),sQuery(id+"F6.wireOp",EDGE,"E18.top"),sQuery(id+"F6.wireOp",EDGE,"E18.left"),sQuery(id+"F6.wireOp",EDGE,"E18.right"),sQuery(id+"F14.wireOp",EDGE,"E26"),sQuery(id+"F14.wireOp",EDGE,"E27"),sQuery(id+"F14.wireOp",EDGE,"E28"),sQuery(id+"F14.wireOp",EDGE,"E29"),sQuery(id+"F14.wireOp",EDGE,"E30"),sQuery(id+"F14.wireOp",EDGE,"E31")])],"isStart":true}),makeQuery(id+"F20.opExtrude","SWEPT_FACE",FACE,{"disambiguationData":[OSD([sQuery(id+"F18.wireOp",EDGE,"E50")])]})]});
            fillet(context, id + "F24", {"entities" : qUnion([Q0, Q1, Q2, Q3, Q4, Q5]), "radius" : 2 * mm, "tangentPropagation" : true, "allowEdgeOverflow" : false});
        }
        {
            var Q0;
            Q0=qCreatedBy(makeId("Front.planeOp"),FACE);
            var sketch = newSketch(context, id + "F25", { "sketchPlane" : qUnion([Q0])});
            skLineSegment(sketch, "E52.bottom", {"start": v(131.01, 39.57) * mm, "end": v(157.3, 39.57) * mm});
            skLineSegment(sketch, "E52.top", {"start": v(131.01, 8.07) * mm, "end": v(157.3, 8.07) * mm});
            skLineSegment(sketch, "E52.left", {"start": v(131.01, 39.57) * mm, "end": v(131.01, 8.07) * mm});
            skLineSegment(sketch, "E52.right", {"start": v(157.3, 39.57) * mm, "end": v(157.3, 8.07) * mm});
            skLineSegment(sketch, "E53", {"start": v(131.01, 39.57) * mm, "end": v(125.8, 39.57) * mm});
            skLineSegment(sketch, "E54", {"start": v(125.8, 39.57) * mm, "end": v(125.8, 33.98) * mm});
            skLineSegment(sketch, "E55", {"start": v(125.8, 33.98) * mm, "end": v(131.01, 33.98) * mm});
            skLineSegment(sketch, "E56", {"start": v(157.3, 13.66) * mm, "end": v(162.5, 13.66) * mm});
            skLineSegment(sketch, "E57", {"start": v(162.5, 13.66) * mm, "end": v(162.5, 8.07) * mm});
            skLineSegment(sketch, "E58", {"start": v(162.5, 8.07) * mm, "end": v(157.3, 8.07) * mm});
            skSolve(sketch);
        }
        {
            var Q0;
            Q0=qSketchRegion(id+"F25",true);
            extrude(context, id + "F26", {"entities" : qUnion([Q0]), "depth" : 1.57 * mm, "offsetDistance" : 25.4 * mm});
        }
        {
            var Q0;
            Q0=makeQuery(id+"F26.opExtrude","CAP_FACE",FACE,{"disambiguationData":[OSD([sQuery(id+"F25.wireOp",EDGE,"E52.bottom"),sQuery(id+"F25.wireOp",EDGE,"E52.top"),sQuery(id+"F25.wireOp",EDGE,"E52.left"),sQuery(id+"F25.wireOp",EDGE,"E52.right"),sQuery(id+"F25.wireOp",EDGE,"E53"),sQuery(id+"F25.wireOp",EDGE,"E54"),sQuery(id+"F25.wireOp",EDGE,"E55"),sQuery(id+"F25.wireOp",EDGE,"E56"),sQuery(id+"F25.wireOp",EDGE,"E57"),sQuery(id+"F25.wireOp",EDGE,"E58")])],"isStart":false});
            var sketch = newSketch(context, id + "F27", { "sketchPlane" : qUnion([Q0])});
            skCircle(sketch, "E59", {"center": v(135.2, 18.8) * mm, "radius": 2.8 * mm});
            skCircle(sketch, "E60", {"center": v(144.15, 18.8) * mm, "radius": 2.8 * mm});
            skCircle(sketch, "E61", {"center": v(153.1, 18.8) * mm, "radius": 2.8 * mm});
            skLineSegment(sketch, "E62", {"start": v(135.2, 18.8) * mm, "end": v(153.1, 18.8) * mm, "construction": true});
            skLineSegment(sketch, "E63", {"start": v(144.15, 39.57) * mm, "end": v(144.15, 8.07) * mm, "construction": true});
            skSolve(sketch);
        }
        {
            var Q0;
            Q0=qSketchRegion(id+"F27",true);
            extrude(context, id + "F28", {"entities" : qUnion([Q0]), "operationType" : NewBodyOperationType.ADD, "depth" : 4.24 * mm, "offsetDistance" : 25.4 * mm});
        }
        {
            var Q0;
            Q0=qCreatedBy(makeId("Right.planeOp"),FACE);
            var sketch = newSketch(context, id + "F29", { "sketchPlane" : qUnion([Q0])});
            skLineSegment(sketch, "E64", {"start": v(76.14, 16.97) * mm, "end": v(76.14, 67.69) * mm});
            skLineSegment(sketch, "E65", {"start": v(76.14, 67.69) * mm, "end": v(48.15, 67.69) * mm});
            skLineSegment(sketch, "E66", {"start": v(48.15, 67.69) * mm, "end": v(66.62, 16.97) * mm});
            skLineSegment(sketch, "E67", {"start": v(66.62, 16.97) * mm, "end": v(76.14, 16.97) * mm});
            skSolve(sketch);
        }
        {
            var Q0;
            Q0=makeQuery(id+"F29.imprint","IMPRINT",FACE,{"disambiguationData":[TD([[makeQuery(id+"F29.imprint","IMPRINT",EDGE,{"derivedFrom":sQuery(id+"F29.wireOp",EDGE,"E64")}),1.0]])]});
            extrude(context, id + "F30", {"entities" : qUnion([Q0]), "endBound" : BoundingType.SYMMETRIC, "depth" : 53.97 * mm, "offsetDistance" : 25.4 * mm});
        }
        {
            var Q0;
            Q0=makeQuery(id+"F30.opExtrude","SWEPT_FACE",FACE,{"disambiguationData":[OSD([sQuery(id+"F29.wireOp",EDGE,"E65")])]});
            shell(context, id + "F31", {"entities" : qUnion([Q0]), "thickness" : 3 * mm});
        }
        {
            var Q0;
            Q0=makeQuery(id+"F30.opExtrude","SWEPT_FACE",FACE,{"disambiguationData":[OSD([sQuery(id+"F29.wireOp",EDGE,"E66")])]});
            var sketch = newSketch(context, id + "F32", { "sketchPlane" : qUnion([Q0])});
            skLineSegment(sketch, "E68.bottom", {"start": v(-20.96, 41.1) * mm, "end": v(20.96, 41.1) * mm});
            skLineSegment(sketch, "E68.top", {"start": v(-20.96, -0.8) * mm, "end": v(20.95, -0.8) * mm});
            skLineSegment(sketch, "E68.left", {"start": v(-20.95, 41.1) * mm, "end": v(-20.96, -0.8) * mm});
            skLineSegment(sketch, "E68.right", {"start": v(20.96, 41.1) * mm, "end": v(20.95, -0.8) * mm});
            skPoint(sketch, "E68.middle", {"position": v(0, 20.15) * mm});
            skPoint(sketch, "E68.middle.positionSnap0", {"position": v(0, 47.14) * mm});
            skPoint(sketch, "E68.centerSnap0", {"position": v(0, 47.14) * mm});
            skLineSegment(sketch, "E69", {"start": v(0, 47.14) * mm, "end": v(0, -6.84) * mm, "construction": true});
            skSolve(sketch);
        }
        {
            var Q0;
            Q0=qSketchRegion(id+"F32",true);
            extrude(context, id + "F33", {"entities" : qUnion([Q0]), "operationType" : NewBodyOperationType.REMOVE, "oppositeDirection" : true, "depth" : 1.5 * mm, "offsetDistance" : 25.4 * mm});
        }
        {
            var Q0;
            Q0=makeQuery(id+"F30.opExtrude","SWEPT_EDGE",EDGE,{"disambiguationData":[OSD([sQuery(id+"F29.wireOp",EDGE,"E66"),sQuery(id+"F29.wireOp",EDGE,"E67")])]});
            fillet(context, id + "F34", {"entities" : qUnion([Q0]), "radius" : 7.54 * mm, "tangentPropagation" : true, "allowEdgeOverflow" : false});
        }
        {
            var Q0;
            Q0=makeQuery(id+"F30.opExtrude","CAP_EDGE",EDGE,{"disambiguationData":[OSD([sQuery(id+"F29.wireOp",EDGE,"E66")])],"isStart":true});
            var Q1;
            Q1=makeQuery(id+"F30.opExtrude","CAP_EDGE",EDGE,{"disambiguationData":[OSD([sQuery(id+"F29.wireOp",EDGE,"E66")])],"isStart":false});
            fillet(context, id + "F35", {"entities" : qUnion([Q0, Q1]), "radius" : 5 * mm, "tangentPropagation" : true, "allowEdgeOverflow" : false});
        }
        {
            var Q0;
            Q0=makeQuery(id+"F33.boolean.opBoolean","COPY",EDGE,{"derivedFrom":makeQuery(id+"F33.opExtrude","SWEPT_EDGE",EDGE,{"disambiguationData":[OSD([sQuery(id+"F32.wireOp",EDGE,"E68.bottom"),sQuery(id+"F32.wireOp",EDGE,"E68.left")])]})});
            var Q1;
            Q1=makeQuery(id+"F33.boolean.opBoolean","COPY",EDGE,{"derivedFrom":makeQuery(id+"F33.opExtrude","SWEPT_EDGE",EDGE,{"disambiguationData":[OSD([sQuery(id+"F32.wireOp",EDGE,"E68.bottom"),sQuery(id+"F32.wireOp",EDGE,"E68.right")])]})});
            var Q2;
            Q2=makeQuery(id+"F33.boolean.opBoolean","COPY",EDGE,{"derivedFrom":makeQuery(id+"F33.opExtrude","SWEPT_EDGE",EDGE,{"disambiguationData":[OSD([sQuery(id+"F32.wireOp",EDGE,"E68.top"),sQuery(id+"F32.wireOp",EDGE,"E68.right")])]})});
            var Q3;
            Q3=makeQuery(id+"F33.boolean.opBoolean","COPY",EDGE,{"derivedFrom":makeQuery(id+"F33.opExtrude","SWEPT_EDGE",EDGE,{"disambiguationData":[OSD([sQuery(id+"F32.wireOp",EDGE,"E68.top"),sQuery(id+"F32.wireOp",EDGE,"E68.left")])]})});
            fillet(context, id + "F36", {"entities" : qUnion([Q0, Q1, Q2, Q3]), "radius" : 0.79 * mm, "tangentPropagation" : true, "allowEdgeOverflow" : false});
        }
        {
            var Q0;
            Q0=makeQuery(id+"F33.boolean.opBoolean","COPY",EDGE,{"derivedFrom":makeQuery(id+"F33.opExtrude","CAP_EDGE",EDGE,{"disambiguationData":[OSD([sQuery(id+"F32.wireOp",EDGE,"E68.top")])],"isStart":false})});
            fillet(context, id + "F37", {"entities" : qUnion([Q0]), "radius" : 0.79 * mm, "tangentPropagation" : true, "allowEdgeOverflow" : false});
        }
        {
            var Q0;
            Q0=makeQuery(id+"F31.opShell","OFFSET_EDGE",EDGE,{"disambiguationData":[OSD([sQuery(id+"F29.wireOp",EDGE,"E66"),sQuery(id+"F29.wireOp",EDGE,"E67")])]});
            fillet(context, id + "F38", {"entities" : qUnion([Q0]), "radius" : 2 * mm, "tangentPropagation" : true, "allowEdgeOverflow" : false});
        }
        {
            var Q0;
            {var subQ0=sQuery(id+"F29.wireOp",EDGE,"E66");Q0=makeQuery(id+"F31.opShell","OFFSET_EDGE",EDGE,{"disambiguationData":[OSD([subQ0]),TDD([makeQuery(id+"F30.opExtrude","CAP_EDGE",EDGE,{"disambiguationData":[OSD([subQ0])],"isStart":false})])]});}
            var Q1;
            {var subQ0=sQuery(id+"F29.wireOp",EDGE,"E66");Q1=makeQuery(id+"F31.opShell","OFFSET_EDGE",EDGE,{"disambiguationData":[OSD([subQ0]),TDD([makeQuery(id+"F30.opExtrude","CAP_EDGE",EDGE,{"disambiguationData":[OSD([subQ0])],"isStart":true})])]});}
            fillet(context, id + "F39", {"entities" : qUnion([Q0, Q1]), "radius" : 2 * mm, "tangentPropagation" : true, "allowEdgeOverflow" : false});
        }
        {
            var Q0;
            Q0=makeQuery(id+"F30.opExtrude","SWEPT_FACE",FACE,{"disambiguationData":[OSD([sQuery(id+"F29.wireOp",EDGE,"E66")])]});
            var sketch = newSketch(context, id + "F40", { "sketchPlane" : qUnion([Q0])});
            skLineSegment(sketch, "E70", {"start": v(-10.64, -0.02) * mm, "end": v(2.06, -0.02) * mm});
            skLineSegment(sketch, "E71", {"start": v(-10.64, 12.68) * mm, "end": v(2.06, 12.68) * mm});
            skArc(sketch, "E72", {"start": v(-10.64, -0.02) * mm, "mid": v(-17, 6.33) * mm, "end": v(-10.64, 12.68) * mm});
            skArc(sketch, "E73", {"start": v(2.06, -0.02) * mm, "mid": v(8.4, 6.33) * mm, "end": v(2.06, 12.68) * mm});
            skSolve(sketch);
        }
        {
            var Q0;
            Q0=makeQuery(id+"F40.imprint","IMPRINT",FACE,{"disambiguationData":[TD([[makeQuery(id+"F40.imprint","IMPRINT",EDGE,{"derivedFrom":sQuery(id+"F40.wireOp",EDGE,"E70")}),1.0]])]});
            extrude(context, id + "F41", {"entities" : qUnion([Q0]), "operationType" : NewBodyOperationType.REMOVE, "endBound" : BoundingType.THROUGH_ALL, "oppositeDirection" : true, "depth" : 25.4 * mm, "offsetDistance" : 25.4 * mm});
        }
        {
            var Q0;
            Q0=makeQuery(id+"F30.opExtrude","CAP_FACE",FACE,{"disambiguationData":[OSD([sQuery(id+"F29.wireOp",EDGE,"E64"),sQuery(id+"F29.wireOp",EDGE,"E65"),sQuery(id+"F29.wireOp",EDGE,"E66"),sQuery(id+"F29.wireOp",EDGE,"E67")])],"isStart":true});
            var sketch = newSketch(context, id + "F42", { "sketchPlane" : qUnion([Q0])});
            skCircle(sketch, "E74", {"center": v(-72.97, 31.5) * mm, "radius": 3.18 * mm});
            skLineSegment(sketch, "E75", {"start": v(-72.97, 34.67) * mm, "end": v(-76.14, 34.67) * mm});
            skLineSegment(sketch, "E76", {"start": v(-76.14, 34.67) * mm, "end": v(-76.14, 28.32) * mm});
            skLineSegment(sketch, "E77", {"start": v(-76.14, 28.32) * mm, "end": v(-72.97, 28.32) * mm});
            skSolve(sketch);
        }
        {
            var Q0;
            {var subQ0=sQuery(id+"F42.wireOp",EDGE,"E74");var subQ1=makeQuery(id+"F42.imprint","INTERSECT",VERTEX,{"derivedFrom":[subQ0,sQuery(id+"F42.wireOp",EDGE,"E75")]});Q0=makeQuery(id+"F42.imprint","IMPRINT",FACE,{"disambiguationData":[TD([[makeQuery(id+"F42.imprint","IMPRINT",EDGE,{"disambiguationData":[TD([[subQ1,-1.0]])],"derivedFrom":subQ0}),1.0]])]});}
            var Q1;
            {var subQ0=sQuery(id+"F42.wireOp",EDGE,"E77");Q1=makeQuery(id+"F42.imprint","IMPRINT",FACE,{"disambiguationData":[TD([[makeQuery(id+"F42.imprint","IMPRINT",EDGE,{"derivedFrom":subQ0}),1.0]])]});}
            var Q2;
            {var subQ0=sQuery(id+"F42.wireOp",EDGE,"E75");Q2=makeQuery(id+"F42.imprint","IMPRINT",FACE,{"disambiguationData":[TD([[makeQuery(id+"F42.imprint","IMPRINT",EDGE,{"derivedFrom":subQ0}),1.0]])]});}
            extrude(context, id + "F43", {"entities" : qUnion([Q0, Q1, Q2]), "operationType" : NewBodyOperationType.REMOVE, "endBound" : BoundingType.THROUGH_ALL, "oppositeDirection" : true, "depth" : 25.4 * mm, "offsetDistance" : 25.4 * mm});
        }
        {
            var Q0;
            Q0=makeQuery(id+"F43.boolean.opBoolean","INTERSECT",EDGE,{"disambiguationData":[OD(1.0)],"derivedFrom":[makeQuery(id+"F31.opShell","OFFSET_FACE",FACE,{"disambiguationData":[OSD([sQuery(id+"F29.wireOp",EDGE,"E64")])]}),makeQuery(id+"F43.opExtrude","SWEPT_FACE",FACE,{"disambiguationData":[OSD([sQuery(id+"F42.wireOp",EDGE,"E74")])]})]});
            var Q1;
            Q1=makeQuery(id+"F43.boolean.opBoolean","INTERSECT",EDGE,{"disambiguationData":[OD(0.0)],"derivedFrom":[makeQuery(id+"F31.opShell","OFFSET_FACE",FACE,{"disambiguationData":[OSD([sQuery(id+"F29.wireOp",EDGE,"E64")])]}),makeQuery(id+"F43.opExtrude","SWEPT_FACE",FACE,{"disambiguationData":[OSD([sQuery(id+"F42.wireOp",EDGE,"E74")])]})]});
            var Q2;
            Q2=makeQuery(id+"F43.boolean.opBoolean","INTERSECT",EDGE,{"disambiguationData":[OD(2.0)],"derivedFrom":[makeQuery(id+"F31.opShell","OFFSET_FACE",FACE,{"disambiguationData":[OSD([sQuery(id+"F29.wireOp",EDGE,"E64")])]}),makeQuery(id+"F43.opExtrude","SWEPT_FACE",FACE,{"disambiguationData":[OSD([sQuery(id+"F42.wireOp",EDGE,"E74")])]})]});
            var Q3;
            Q3=makeQuery(id+"F43.boolean.opBoolean","INTERSECT",EDGE,{"disambiguationData":[OD(3.0)],"derivedFrom":[makeQuery(id+"F31.opShell","OFFSET_FACE",FACE,{"disambiguationData":[OSD([sQuery(id+"F29.wireOp",EDGE,"E64")])]}),makeQuery(id+"F43.opExtrude","SWEPT_FACE",FACE,{"disambiguationData":[OSD([sQuery(id+"F42.wireOp",EDGE,"E74")])]})]});
            fillet(context, id + "F44", {"entities" : qUnion([Q0, Q1, Q2, Q3]), "radius" : 0.76 * mm, "tangentPropagation" : true, "allowEdgeOverflow" : false});
        }
    });
